# Revit family: 2059866
name_source: partatom
category: Lighting Fixtures
revit_build: Autodesk Revit 2017 (Build: 20160225_1515(x64)
units: mm (PartAtom-declared; Revit-internal decimal feet)

## family parameters
Always vertical = No
Cut with Voids When Loaded = No
Light Source = No
Part Type = Normal
Room Calculation Point = No
Round Connector Dimension = Use Diameter
Shared = No
Work Plane-Based = Yes

## types (1)
- 2059866 BEACON MINOR II 4K FLD L1 WHT
    Apparent Load = 10 VA
    Assembly Code = D5020200
    AssetType = Fixed
    Default Elevation = 0 mm  [stored 0 ft]
    Description = Integrated AC LED spotlight, white RAL 9016, compact and minimalist design, ideal for retail and display applications, die-cast aluminium body, passive cooling heatsink, beam angle: 44° flood, optics: polycarbonate reflector, colour temperature: 4000K Neutral White, total system power: 10W, total fixture output: 886lm, luminaire efficacy: 89lm/W, LOR: 100%, colour rendering: Ra 80 typical, LED Chromacity: 3 step MacAdam ellipse, lifetime: 48,000 hours at L70B50, energy class: A++, A+, A, IR/UV free light source without heat radiation, operating voltage: 220-240V / 50-60Hz, mains dimmable, trailing or leading edge dimmable, power factor: 0.9 electrical protection: CLASS I, 3-circuit track adaptor, suitable for Concord Lytespan 3 track, ingress protection rating: IP20, suitable for internal environment only, horizontal rotation: 355°, vertical tilt: 90°, dimensions: Ø79x118x168mm, weight: 0.40kg.
    Diameter_SYL = 79 mm
    DocumentationLiterature = http://www.sylvania-lighting.com
    DurationUnit = hours
    ElectricShockClassification = Class I
    ExpectedLife = 0
    IfcExportAs = IfcLightFixtureType
    IfcExportType = IfcLightFixtureType
    ImpactProtectionIndex = IK02
    IngressProtection = IP20
    InputNominalFrequency = 50/60Hz
    InputVoltage = 220-240 V AC
    Keynote = 16500
    Lamp = LED
    LampColourRenderingIndex = 80
    LampColourTemperature = 4000 K
    LampNominalLuminous = 886 lm
    LampsType = LED
    LightOutputRatio = 100
    LuminousEfficacy = 89 lm/W
    Manufacturer = Feilo Sylvania
    ManufacturerName = Feilo Sylvania
    Material = aluminium housing
    Material_1_SYL = Aluminum_Sylvania_Beacon_White
    Material_2_SYL = <By Category>
    Material_3_SYL = <By Category>
    Material_4_SYL = <By Category>
    Model = BEACON MINOR II 4K FLD L1 WHT
    ModelNumber = 2059866
    ModelReference = BEACON MINOR II 4K FLD L1 WHT
    Name = BEACON MINOR II 4K FLD L1 WHT
    NominalHeight = 140 mm  [stored 0.459318 ft]
    NominalLength = 118 mm
    NominalWidth = 0 mm  [stored 0 ft]
    PowerConsumption = 10 W
    PowerFactor = 0
    TypeHeadAndStand_SYL = Rotateable Head&Stand : 2059866 BEACON MINOR II 4K FLD L1 WHT
    TypeName = BEACON MINOR II 4K FLD L1 WHT
    URL = http://www.sylvania-lighting.com
    Voltage = 230 V
    Weight = 0.915 kg

note: [stored X ft] marks values corroborated as IEEE doubles in the binary element streams (Revit-internal decimal feet)

## geometry (parser evidence)
native form markers: Sweep x9
no freeform markers — native parametric forms only
